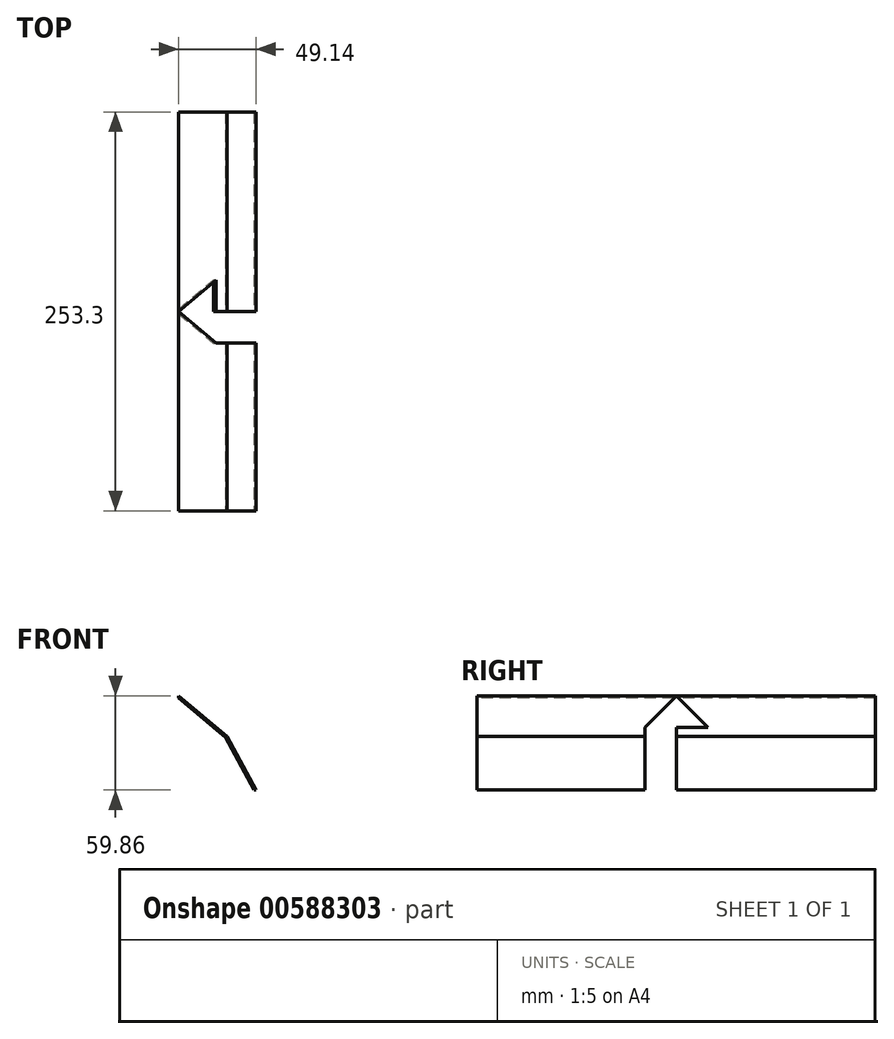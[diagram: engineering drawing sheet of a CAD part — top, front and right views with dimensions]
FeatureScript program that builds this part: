
annotation { "Feature Type Name" : "Feature", "Feature Type Description" : "" }
export const myFeature = defineFeature(function(context is Context, id is Id, definition is map)
    precondition{}
    {
        {
            var Q0;
            Q0=qCreatedBy(makeId("Front.planeOp"),FACE);
            var sketch = newSketch(context, id + "F0", { "sketchPlane" : qUnion([Q0])});
            skLineSegment(sketch, "E0", {"start": v(-97.77, 76.26) * mm, "end": v(-79.77, 42.96) * mm});
            skLineSegment(sketch, "E1", {"start": v(-127.77, 101.51) * mm, "end": v(-97.77, 76.26) * mm});
            skLineSegment(sketch, "E2", {"start": v(-127.77, 101.51) * mm, "end": v(-157.77, 76.26) * mm});
            skLineSegment(sketch, "E3", {"start": v(-175.77, 42.96) * mm, "end": v(-157.77, 76.26) * mm});
            skLineSegment(sketch, "E4", {"start": v(-175.77, 42.96) * mm, "end": v(-178.77, 42.96) * mm});
            skLineSegment(sketch, "E5", {"start": v(-79.77, 42.96) * mm, "end": v(-76.77, 42.96) * mm});
            skLineSegment(sketch, "E6.0", {"start": v(-96.98, 76.9) * mm, "end": v(-78.89, 43.44) * mm});
            skLineSegment(sketch, "E6.1", {"start": v(-127.77, 102.82) * mm, "end": v(-96.98, 76.9) * mm});
            skLineSegment(sketch, "E6.2", {"start": v(-127.77, 102.82) * mm, "end": v(-158.56, 76.9) * mm});
            skLineSegment(sketch, "E6.3", {"start": v(-177.84, 41.23) * mm, "end": v(-158.56, 76.9) * mm});
            skLineSegment(sketch, "E7", {"start": v(-175.77, 42.96) * mm, "end": v(-79.77, 42.96) * mm});
            skLineSegment(sketch, "E8", {"start": v(-78.89, 43.44) * mm, "end": v(-78.63, 42.96) * mm});
            skPoint(sketch, "E8.endSnap0", {"position": v(-78.27, 42.96) * mm});
            skPoint(sketch, "E9.orphan", {"position": v(-78.27, 42.3) * mm});
            skLineSegment(sketch, "E10", {"start": v(-175.77, 42.96) * mm, "end": v(-176.9, 42.96) * mm});
            skLineSegment(sketch, "E11", {"start": v(-127.77, 102.82) * mm, "end": v(-191.71, 102.82) * mm});
            skLineSegment(sketch, "E12", {"start": v(-127.77, 102.82) * mm, "end": v(-66.72, 102.82) * mm});
            skLineSegment(sketch, "E13", {"start": v(-176.9, 42.96) * mm, "end": v(-176.9, 107.35) * mm});
            skLineSegment(sketch, "E14", {"start": v(-78.63, 42.96) * mm, "end": v(-78.63, 110.13) * mm});
            skSolve(sketch);
        }
        {
            var Q0;
            Q0=makeQuery(id+"F0.imprint","IMPRINT",FACE,{"disambiguationData":[TD([[makeQuery(id+"F0.imprint","IMPRINT",EDGE,{"derivedFrom":sQuery(id+"F0.wireOp",EDGE,"E6.0")}),1.0]])]});
            var Q1;
            Q1=makeQuery(id+"F0.imprint","IMPRINT",FACE,{"disambiguationData":[TD([[makeQuery(id+"F0.imprint","IMPRINT",EDGE,{"derivedFrom":sQuery(id+"F0.wireOp",EDGE,"E0")}),-1.0]])]});
            var Q2;
            {var subQ5=sQuery(id+"F0.wireOp",EDGE,"E0");Q2=makeQuery(id+"F0.imprint","IMPRINT",FACE,{"disambiguationData":[TD([[makeQuery(id+"F0.imprint","IMPRINT",EDGE,{"derivedFrom":subQ5}),1.0]])]});}
            var Q3;
            {var subQ0=sQuery(id+"F0.wireOp",EDGE,"E6.2");Q3=makeQuery(id+"F0.imprint","IMPRINT",FACE,{"disambiguationData":[TD([[makeQuery(id+"F0.imprint","IMPRINT",EDGE,{"derivedFrom":subQ0}),-1.0]])]});}
            extrude(context, id + "F1", {"entities" : qUnion([Q0, Q1, Q2, Q3]), "oppositeDirection" : true, "depth" : 247.3 * mm, "offsetDistance" : 25 * mm});
        }
        {
            var Q0;
            Q0=makeQuery(id+"F1.opExtrude","SWEPT_FACE",FACE,{"disambiguationData":[OSD([sQuery(id+"F0.wireOp",EDGE,"E14")])]});
            var sketch = newSketch(context, id + "F2", { "sketchPlane" : qUnion([Q0])});
            skLineSegment(sketch, "E15.0", {"start": v(247.3, 102.82) * mm, "end": v(0, 102.82) * mm});
            skLineSegment(sketch, "E16.0", {"start": v(247.3, 42.96) * mm, "end": v(247.3, 102.82) * mm});
            skLineSegment(sketch, "E17.0", {"start": v(247.3, 42.96) * mm, "end": v(0, 42.96) * mm});
            skLineSegment(sketch, "E18.0", {"start": v(0, 42.96) * mm, "end": v(0, 110.13) * mm});
            skPoint(sketch, "E19.start.orphan", {"position": v(123.65, 102.82) * mm});
            skLineSegment(sketch, "E20", {"start": v(123.65, 102.82) * mm, "end": v(123.65, 42.96) * mm});
            skLineSegment(sketch, "E21", {"start": v(123.65, 102.82) * mm, "end": v(123.65, 84.6) * mm});
            skLineSegment(sketch, "E22", {"start": v(123.65, 102.82) * mm, "end": v(123.65, 82.82) * mm});
            skLineSegment(sketch, "E23", {"start": v(123.65, 82.82) * mm, "end": v(103.65, 82.82) * mm});
            skLineSegment(sketch, "E24", {"start": v(103.65, 82.82) * mm, "end": v(123.65, 102.82) * mm});
            skLineSegment(sketch, "E25", {"start": v(123.65, 82.82) * mm, "end": v(143.65, 82.82) * mm});
            skLineSegment(sketch, "E26", {"start": v(143.65, 82.82) * mm, "end": v(123.65, 102.82) * mm});
            skLineSegment(sketch, "E27", {"start": v(143.65, 82.82) * mm, "end": v(143.65, 42.96) * mm});
            skSolve(sketch);
        }
        {
            var Q0;
            Q0=makeQuery(id+"F0.imprint","IMPRINT",FACE,{"disambiguationData":[TD([[makeQuery(id+"F0.imprint","IMPRINT",EDGE,{"derivedFrom":sQuery(id+"F0.wireOp",EDGE,"E6.0")}),1.0]])]});
            extrude(context, id + "F3", {"entities" : qUnion([Q0]), "operationType" : NewBodyOperationType.REMOVE, "oppositeDirection" : true, "depth" : 300 * mm, "offsetDistance" : 25 * mm});
        }
        {
            var Q0;
            {var subQ3=sQuery(id+"F2.wireOp",EDGE,"E23");Q0=makeQuery(id+"F2.imprint","IMPRINT",FACE,{"disambiguationData":[TD([[makeQuery(id+"F2.imprint","IMPRINT",EDGE,{"derivedFrom":subQ3}),-1.0]])]});}
            extrude(context, id + "F4", {"entities" : qUnion([Q0]), "operationType" : NewBodyOperationType.ADD, "oppositeDirection" : true, "depth" : 61.9 * mm, "offsetDistance" : 25 * mm});
        }
        {
            var Q0;
            Q0=makeQuery(id+"F4.opExtrude","SWEPT_FACE",FACE,{"disambiguationData":[OSD([sQuery(id+"F2.wireOp",EDGE,"E23")])]});
            extrude(context, id + "F5", {"entities" : qUnion([Q0]), "operationType" : NewBodyOperationType.ADD, "depth" : 40 * mm, "offsetDistance" : 25 * mm});
        }
        {
            var Q0;
            Q0=makeQuery(id+"F5.opExtrude","CAP_FACE",FACE,{"disambiguationData":[OSD([sQuery(id+"F2.wireOp",EDGE,"E23")])],"isStart":false});
            extrude(context, id + "F6", {"entities" : qUnion([Q0]), "operationType" : NewBodyOperationType.REMOVE, "oppositeDirection" : true, "depth" : 40 * mm, "offsetDistance" : 25 * mm});
        }
        {
            var Q0;
            Q0=makeQuery(id+"F0.imprint","IMPRINT",FACE,{"disambiguationData":[TD([[makeQuery(id+"F0.imprint","IMPRINT",EDGE,{"derivedFrom":sQuery(id+"F0.wireOp",EDGE,"E0")}),-1.0]])]});
            extrude(context, id + "F7", {"entities" : qUnion([Q0]), "operationType" : NewBodyOperationType.REMOVE, "oppositeDirection" : true, "depth" : 300 * mm, "offsetDistance" : 25 * mm});
        }
        {
            var Q0;
            {var subQ0=sQuery(id+"F0.wireOp",EDGE,"E6.2");Q0=makeQuery(id+"F0.imprint","IMPRINT",FACE,{"disambiguationData":[TD([[makeQuery(id+"F0.imprint","IMPRINT",EDGE,{"derivedFrom":subQ0}),-1.0]])]});}
            extrude(context, id + "F8", {"entities" : qUnion([Q0]), "operationType" : NewBodyOperationType.REMOVE, "oppositeDirection" : true, "depth" : 300 * mm, "offsetDistance" : 25 * mm});
        }
        {
            var Q0;
            {var subQ5=sQuery(id+"F0.wireOp",EDGE,"E0");Q0=makeQuery(id+"F0.imprint","IMPRINT",FACE,{"disambiguationData":[TD([[makeQuery(id+"F0.imprint","IMPRINT",EDGE,{"derivedFrom":subQ5}),1.0]])]});}
            var sketch = newSketch(context, id + "F9", { "sketchPlane" : qUnion([Q0])});
            skLineSegment(sketch, "E28.0", {"start": v(-127.77, 102.82) * mm, "end": v(-96.98, 76.9) * mm});
            skLineSegment(sketch, "E29.0", {"start": v(-127.77, 101.51) * mm, "end": v(-97.77, 76.26) * mm});
            skLineSegment(sketch, "E30", {"start": v(-127.77, 101.51) * mm, "end": v(-127.77, 102.82) * mm});
            skSolve(sketch);
        }
        {
            var Q0;
            Q0=makeQuery(id+"F9.imprint","IMPRINT",FACE,{"disambiguationData":[TD([[makeQuery(id+"F9.imprint","IMPRINT",EDGE,{"derivedFrom":sQuery(id+"F9.wireOp",EDGE,"E30")}),1.0]])]});
            extrude(context, id + "F10", {"entities" : qUnion([Q0]), "operationType" : NewBodyOperationType.REMOVE, "oppositeDirection" : true, "depth" : 300 * mm, "offsetDistance" : 25 * mm});
        }
        {
            var Q0;
            {var subQ0=sQuery(id+"F2.wireOp",EDGE,"E23");Q0=makeQuery(id+"F5.boolean.opBoolean","MERGE",FACE,{"derivedFrom":[makeQuery(id+"F4.opExtrude","CAP_FACE",FACE,{"disambiguationData":[OSD([sQuery(id+"F2.wireOp",EDGE,"E22"),subQ0,sQuery(id+"F2.wireOp",EDGE,"E24")])],"isStart":true}),makeQuery(id+"F5.opExtrude","SWEPT_FACE",FACE,{"disambiguationData":[OSD([subQ0])]})]});}
            var Q1;
            Q1=makeQuery(id+"F6.boolean.opBoolean","COPY",FACE,{"derivedFrom":makeQuery(id+"F6.opExtrude","SWEPT_FACE",FACE,{"disambiguationData":[OSD([sQuery(id+"F0.wireOp",EDGE,"E6.1"),sQuery(id+"F2.wireOp",EDGE,"E23")])]})});
            extrude(context, id + "F11", {"entities" : qUnion([Q0, Q1]), "operationType" : NewBodyOperationType.REMOVE, "oppositeDirection" : true, "depth" : 25 * mm, "offsetDistance" : 25 * mm});
        }
        {
            var Q0;
            Q0=makeQuery(id+"F11.boolean.opBoolean","COPY",FACE,{"derivedFrom":makeQuery(id+"F11.opExtrude","CAP_FACE",FACE,{"disambiguationData":[OSD([sQuery(id+"F2.wireOp",EDGE,"E22"),sQuery(id+"F2.wireOp",EDGE,"E23"),sQuery(id+"F2.wireOp",EDGE,"E24")])],"isStart":false})});
            extrude(context, id + "F12", {"entities" : qUnion([Q0]), "operationType" : NewBodyOperationType.REMOVE, "oppositeDirection" : true, "depth" : 71.4 * mm, "offsetDistance" : 25 * mm});
        }
        {
            var Q0;
            {var subQ5=sQuery(id+"F0.wireOp",EDGE,"E0");Q0=makeQuery(id+"F0.imprint","IMPRINT",FACE,{"disambiguationData":[TD([[makeQuery(id+"F0.imprint","IMPRINT",EDGE,{"derivedFrom":subQ5}),1.0]])]});}
            extrude(context, id + "F13", {"entities" : qUnion([Q0]), "operationType" : NewBodyOperationType.ADD, "depth" : 3 * mm, "offsetDistance" : 25 * mm});
        }
        {
            var Q0;
            {var subQ3=sQuery(id+"F2.wireOp",EDGE,"E25");Q0=makeQuery(id+"F2.imprint","IMPRINT",FACE,{"disambiguationData":[TD([[makeQuery(id+"F2.imprint","IMPRINT",EDGE,{"derivedFrom":subQ3}),1.0]])]});}
            extrude(context, id + "F14", {"entities" : qUnion([Q0]), "operationType" : NewBodyOperationType.ADD, "oppositeDirection" : true, "depth" : 65.7 * mm, "offsetDistance" : 25 * mm});
        }
        {
            var Q0;
            {var subQ3=sQuery(id+"F2.wireOp",EDGE,"E25");Q0=makeQuery(id+"F2.imprint","IMPRINT",FACE,{"disambiguationData":[TD([[makeQuery(id+"F2.imprint","IMPRINT",EDGE,{"derivedFrom":subQ3}),1.0]])]});}
            extrude(context, id + "F15", {"entities" : qUnion([Q0]), "operationType" : NewBodyOperationType.REMOVE, "oppositeDirection" : true, "depth" : 82.2 * mm, "offsetDistance" : 25 * mm});
        }
        {
            var Q0;
            {var subQ0=sQuery(id+"F2.wireOp",EDGE,"E20");Q0=makeQuery(id+"F2.imprint","IMPRINT",FACE,{"disambiguationData":[TD([[makeQuery(id+"F2.imprint","IMPRINT",EDGE,{"derivedFrom":subQ0}),1.0]])]});}
            extrude(context, id + "F16", {"entities" : qUnion([Q0]), "operationType" : NewBodyOperationType.ADD, "oppositeDirection" : true, "depth" : 52.6 * mm, "offsetDistance" : 25 * mm});
        }
        {
            var Q0;
            {var subQ0=sQuery(id+"F2.wireOp",EDGE,"E20");Q0=makeQuery(id+"F2.imprint","IMPRINT",FACE,{"disambiguationData":[TD([[makeQuery(id+"F2.imprint","IMPRINT",EDGE,{"derivedFrom":subQ0}),1.0]])]});}
            extrude(context, id + "F17", {"entities" : qUnion([Q0]), "operationType" : NewBodyOperationType.REMOVE, "oppositeDirection" : true, "depth" : 121.6 * mm, "offsetDistance" : 25 * mm});
        }
        {
            var Q0;
            Q0=makeQuery(id+"F1.opExtrude","CAP_FACE",FACE,{"disambiguationData":[OSD([sQuery(id+"F0.wireOp",EDGE,"E5"),sQuery(id+"F0.wireOp",EDGE,"E7"),sQuery(id+"F0.wireOp",EDGE,"E10"),sQuery(id+"F0.wireOp",EDGE,"E11"),sQuery(id+"F0.wireOp",EDGE,"E12"),sQuery(id+"F0.wireOp",EDGE,"E13"),sQuery(id+"F0.wireOp",EDGE,"E14")])],"isStart":false});
            extrude(context, id + "F18", {"entities" : qUnion([Q0]), "operationType" : NewBodyOperationType.ADD, "depth" : 3 * mm, "offsetDistance" : 25 * mm});
        }
        {
            var Q0;
            Q0=makeQuery(id+"F13.opExtrude","CAP_FACE",FACE,{"disambiguationData":[OSD([sQuery(id+"F0.wireOp",EDGE,"E0"),sQuery(id+"F0.wireOp",EDGE,"E1"),sQuery(id+"F0.wireOp",EDGE,"E2"),sQuery(id+"F0.wireOp",EDGE,"E3"),sQuery(id+"F0.wireOp",EDGE,"E5"),sQuery(id+"F0.wireOp",EDGE,"E6.0"),sQuery(id+"F0.wireOp",EDGE,"E6.1"),sQuery(id+"F0.wireOp",EDGE,"E6.2"),sQuery(id+"F0.wireOp",EDGE,"E6.3"),sQuery(id+"F0.wireOp",EDGE,"E8"),sQuery(id+"F0.wireOp",EDGE,"E10")])],"isStart":false});
            var sketch = newSketch(context, id + "F19", { "sketchPlane" : qUnion([Q0])});
            skLineSegment(sketch, "E31.0", {"start": v(-127.77, 102.82) * mm, "end": v(-158.56, 76.9) * mm});
            skLineSegment(sketch, "E32.0", {"start": v(-127.77, 101.51) * mm, "end": v(-157.77, 76.26) * mm});
            skLineSegment(sketch, "E33.0", {"start": v(-127.77, 101.51) * mm, "end": v(-97.77, 76.26) * mm});
            skLineSegment(sketch, "E34.0", {"start": v(-127.77, 102.82) * mm, "end": v(-96.98, 76.9) * mm});
            skLineSegment(sketch, "E35", {"start": v(-127.77, 102.82) * mm, "end": v(-127.77, 101.51) * mm});
            skSolve(sketch);
        }
        {
            var Q0;
            Q0=makeQuery(id+"F19.imprint","IMPRINT",FACE,{"disambiguationData":[TD([[makeQuery(id+"F19.imprint","IMPRINT",EDGE,{"derivedFrom":sQuery(id+"F19.wireOp",EDGE,"E31.0")}),1.0]])]});
            extrude(context, id + "F20", {"entities" : qUnion([Q0]), "operationType" : NewBodyOperationType.REMOVE, "oppositeDirection" : true, "depth" : 25 * mm, "offsetDistance" : 25 * mm});
        }
    });
